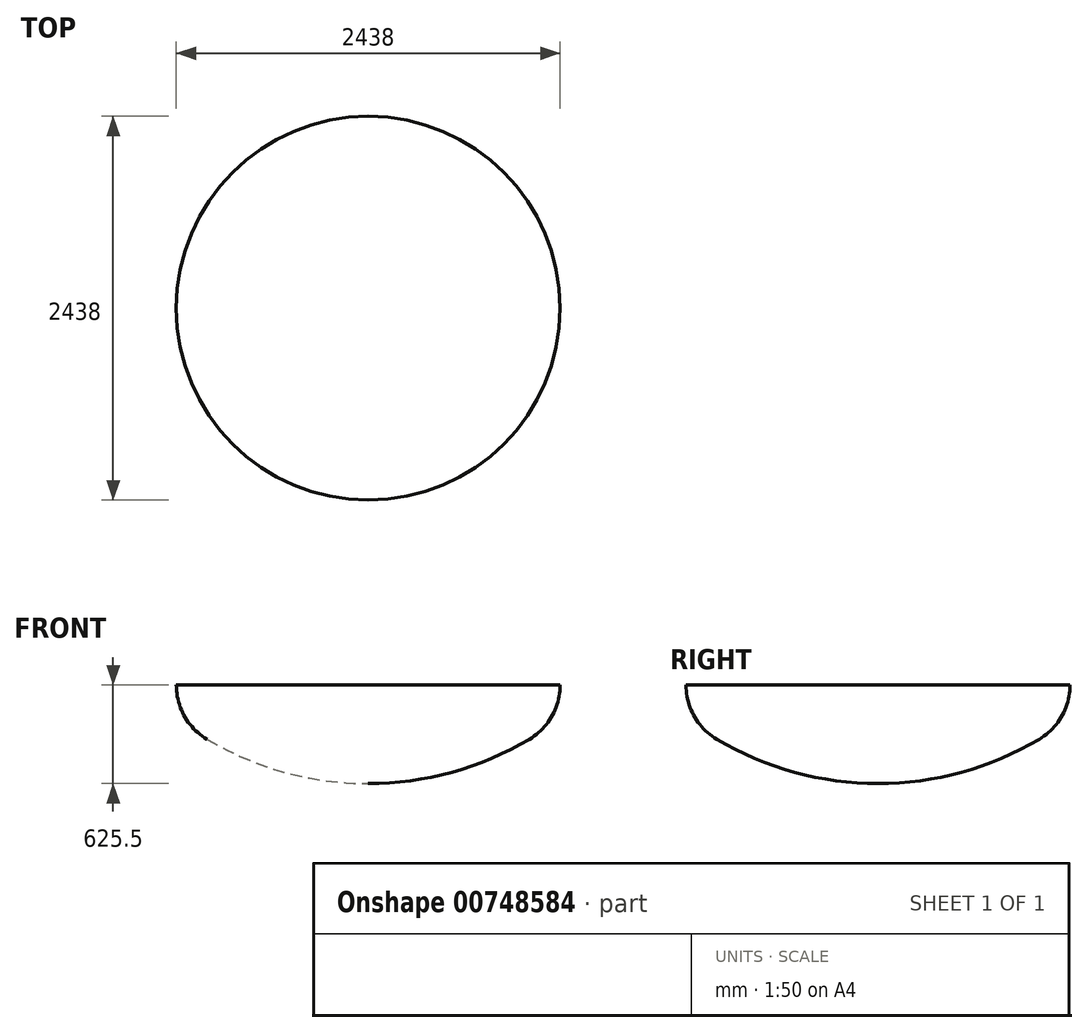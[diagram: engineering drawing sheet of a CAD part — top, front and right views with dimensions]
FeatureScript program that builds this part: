
annotation { "Feature Type Name" : "Feature", "Feature Type Description" : "" }
export const myFeature = defineFeature(function(context is Context, id is Id, definition is map)
    precondition{}
    {
        {
            var Q0;
            Q0=qCreatedBy(makeId("Front.planeOp"),FACE);
            var sketch = newSketch(context, id + "F0", { "sketchPlane" : qUnion([Q0])});
            skArc(sketch, "E0", {"start": v(-1023.75, 281.88) * mm, "mid": v(0, 0) * mm, "end": v(1023.75, 281.88) * mm});
            skArc(sketch, "E1", {"start": v(-1219, 625.5) * mm, "mid": v(-1166.78, 427.9) * mm, "end": v(-1023.75, 281.88) * mm});
            skArc(sketch, "E2", {"start": v(1023.75, 281.88) * mm, "mid": v(1166.78, 427.9) * mm, "end": v(1219, 625.5) * mm});
            skLineSegment(sketch, "E3", {"start": v(-1219, 625.5) * mm, "end": v(1219, 625.5) * mm});
            skLineSegment(sketch, "E4", {"start": v(0, 0) * mm, "end": v(0, 625.5) * mm});
            skSolve(sketch);
        }
        {
            var Q0;
            {var subQ0=sQuery(id+"F0.wireOp",EDGE,"E1");Q0=makeQuery(id+"F0.imprint","IMPRINT",FACE,{"disambiguationData":[TD([[makeQuery(id+"F0.imprint","IMPRINT",EDGE,{"derivedFrom":subQ0}),1.0]])]});}
            var Q1;
            Q1=sQuery(id+"F0.wireOp",EDGE,"E4");
            revolve(context, id + "F1", {"surfaceOperationType" : NewSurfaceOperationType.NEW, "entities" : qUnion([Q0]), "axis" : qUnion([Q1]), "revolveType" : RevolveType.FULL});
        }
    });
